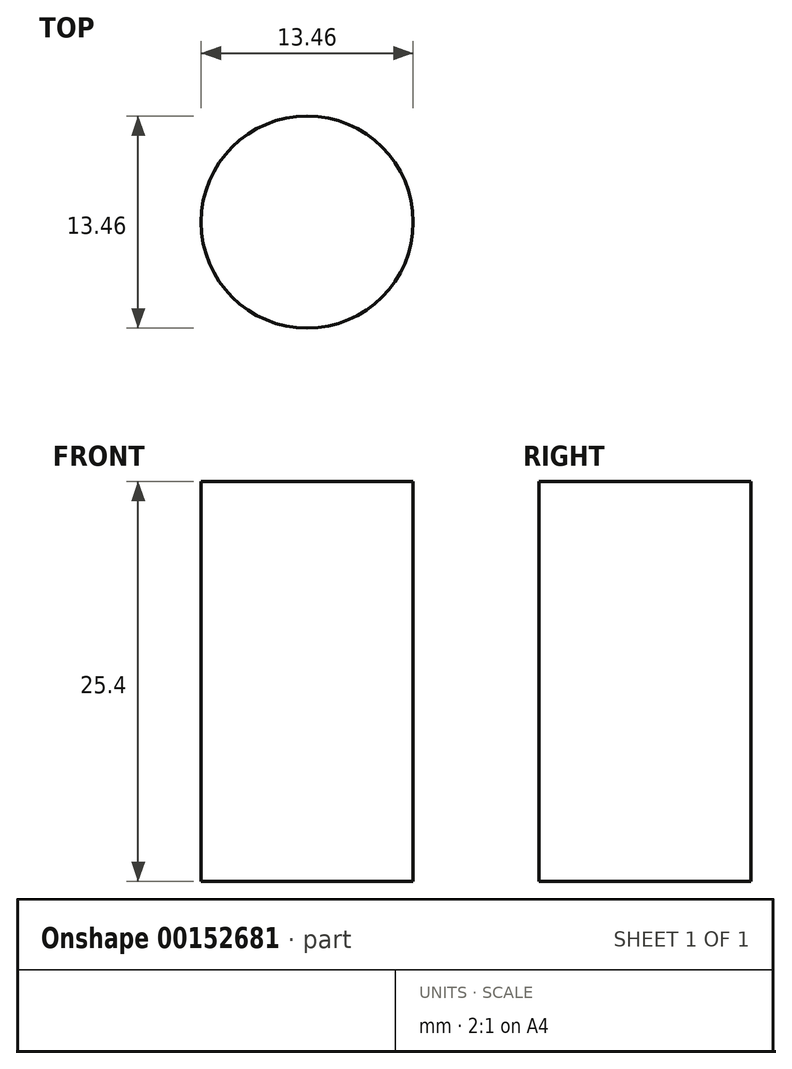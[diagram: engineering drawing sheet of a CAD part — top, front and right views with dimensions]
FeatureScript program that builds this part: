
annotation { "Feature Type Name" : "Feature", "Feature Type Description" : "" }
export const myFeature = defineFeature(function(context is Context, id is Id, definition is map)
    precondition{}
    {
        {
            var Q0;
            Q0=qCreatedBy(makeId("Top.planeOp"),FACE);
            var sketch = newSketch(context, id + "F0", { "sketchPlane" : qUnion([Q0])});
            skCircle(sketch, "E0", {"center": v(0, 0) * mm, "radius": 6.73 * mm});
            skLineSegment(sketch, "E1", {"start": v(0, 0) * mm, "end": v(0, 25.4) * mm, "construction": true});
            skLineSegment(sketch, "E2", {"start": v(0, 25.4) * mm, "end": v(20.67, 25.4) * mm, "construction": true});
            skLineSegment(sketch, "E3", {"start": v(0, 25.4) * mm, "end": v(0, 50.8) * mm, "construction": true});
            skLineSegment(sketch, "E4", {"start": v(-16.54, 50.8) * mm, "end": v(16.54, 50.8) * mm, "construction": true});
            skLineSegment(sketch, "E5", {"start": v(16.54, 50.8) * mm, "end": v(40.93, 36.72) * mm, "construction": true});
            skLineSegment(sketch, "E6", {"start": v(-16.54, 50.8) * mm, "end": v(-40.93, 36.72) * mm, "construction": true});
            skLineSegment(sketch, "E7", {"start": v(20.67, 25.4) * mm, "end": v(16.54, 50.8) * mm, "construction": true});
            skCircle(sketch, "E8", {"center": v(16.54, 50.8) * mm, "radius": 16.54 * mm, "construction": true});
            skCircle(sketch, "E9", {"center": v(-16.54, 50.8) * mm, "radius": 16.54 * mm, "construction": true});
            skCircle(sketch, "E10", {"center": v(20.67, 25.4) * mm, "radius": 9.2 * mm, "construction": true});
            skLineSegment(sketch, "E11", {"start": v(-16.54, 50.8) * mm, "end": v(-20.48, 70.12) * mm, "construction": true});
            skLineSegment(sketch, "E12", {"start": v(-40.93, 36.72) * mm, "end": v(-44.87, 56.04) * mm, "construction": true});
            skLineSegment(sketch, "E13", {"start": v(-44.87, 56.04) * mm, "end": v(-20.48, 70.12) * mm, "construction": true});
            skLineSegment(sketch, "E14", {"start": v(16.54, 50.8) * mm, "end": v(20.48, 70.12) * mm, "construction": true});
            skLineSegment(sketch, "E15", {"start": v(40.93, 36.72) * mm, "end": v(44.87, 56.04) * mm, "construction": true});
            skLineSegment(sketch, "E16", {"start": v(20.48, 70.12) * mm, "end": v(44.87, 56.04) * mm, "construction": true});
            skLineSegment(sketch, "E17", {"start": v(16.54, 50.8) * mm, "end": v(40.93, 50.8) * mm, "construction": true});
            skLineSegment(sketch, "E18", {"start": v(40.93, 50.8) * mm, "end": v(40.93, 36.72) * mm, "construction": true});
            skLineSegment(sketch, "E19", {"start": v(-40.93, 36.72) * mm, "end": v(-40.93, 50.8) * mm, "construction": true});
            skLineSegment(sketch, "E20", {"start": v(-40.93, 50.8) * mm, "end": v(-16.54, 50.8) * mm, "construction": true});
            skLineSegment(sketch, "E21", {"start": v(-20.48, 70.12) * mm, "end": v(-16.51, 70.12) * mm, "construction": true});
            skLineSegment(sketch, "E22", {"start": v(-16.51, 70.12) * mm, "end": v(16.51, 70.12) * mm, "construction": true});
            skLineSegment(sketch, "E23", {"start": v(16.51, 70.12) * mm, "end": v(20.48, 70.12) * mm, "construction": true});
            skLineSegment(sketch, "E24", {"start": v(0, 50.8) * mm, "end": v(0, 70.12) * mm, "construction": true});
            skLineSegment(sketch, "E25", {"start": v(18.51, 60.46) * mm, "end": v(22.4, 59.67) * mm, "construction": true});
            skLineSegment(sketch, "E26", {"start": v(24.1, 68.03) * mm, "end": v(22.4, 59.67) * mm, "construction": true});
            skLineSegment(sketch, "E27", {"start": v(42.9, 46.38) * mm, "end": v(37.46, 47.49) * mm, "construction": true});
            skSolve(sketch);
        }
        {
            var Q0;
            Q0 = qSketchRegion(id + "F0", true);
            extrude(context, id + "F1", {"entities" : qUnion([Q0]), "depth" : 25.4 * mm});
        }
    });
